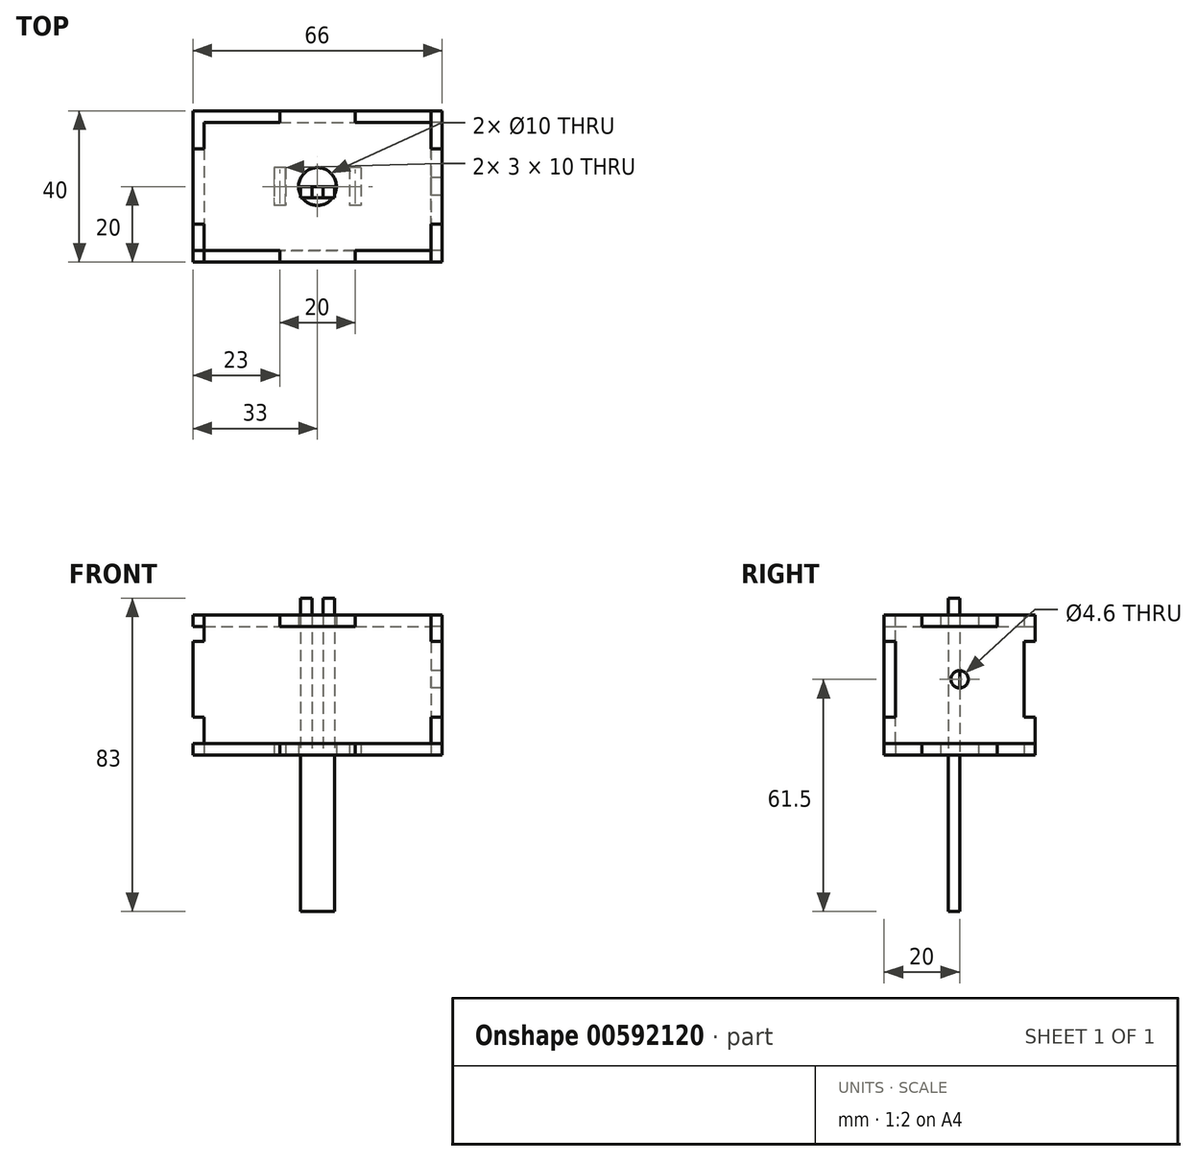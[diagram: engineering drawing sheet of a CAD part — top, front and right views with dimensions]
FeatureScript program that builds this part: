
annotation { "Feature Type Name" : "Feature", "Feature Type Description" : "" }
export const myFeature = defineFeature(function(context is Context, id is Id, definition is map)
    precondition{}
    {
        {
            var Q0;
            Q0=qCreatedBy(makeId("Top.planeOp"),FACE);
            var sketch = newSketch(context, id + "F0", { "sketchPlane" : qUnion([Q0])});
            skLineSegment(sketch, "E0.bottom", {"start": v(33, 20) * mm, "end": v(-33, 20) * mm});
            skLineSegment(sketch, "E0.top", {"start": v(33, -20) * mm, "end": v(-33, -20) * mm});
            skLineSegment(sketch, "E0.left", {"start": v(33, 20) * mm, "end": v(33, -20) * mm});
            skLineSegment(sketch, "E0.right", {"start": v(-33, 20) * mm, "end": v(-33, -20) * mm});
            skLineSegment(sketch, "E1.bottom", {"start": v(-10, 20) * mm, "end": v(10, 20) * mm});
            skLineSegment(sketch, "E1.top", {"start": v(-10, 17) * mm, "end": v(10, 17) * mm});
            skLineSegment(sketch, "E1.left", {"start": v(-10, 20) * mm, "end": v(-10, 17) * mm});
            skLineSegment(sketch, "E1.right", {"start": v(10, 20) * mm, "end": v(10, 17) * mm});
            skLineSegment(sketch, "E2.bottom", {"start": v(33, 10) * mm, "end": v(30, 10) * mm});
            skLineSegment(sketch, "E2.top", {"start": v(33, -10) * mm, "end": v(30, -10) * mm});
            skLineSegment(sketch, "E2.left", {"start": v(33, 10) * mm, "end": v(33, -10) * mm});
            skLineSegment(sketch, "E2.right", {"start": v(30, 10) * mm, "end": v(30, -10) * mm});
            skLineSegment(sketch, "E3.bottom", {"start": v(10, -20) * mm, "end": v(-10, -20) * mm});
            skLineSegment(sketch, "E3.top", {"start": v(10, -17) * mm, "end": v(-10, -17) * mm});
            skLineSegment(sketch, "E3.left", {"start": v(10, -20) * mm, "end": v(10, -17) * mm});
            skLineSegment(sketch, "E3.right", {"start": v(-10, -20) * mm, "end": v(-10, -17) * mm});
            skLineSegment(sketch, "E4.bottom", {"start": v(-33, 10) * mm, "end": v(-30, 10) * mm});
            skLineSegment(sketch, "E4.top", {"start": v(-33, -10) * mm, "end": v(-30, -10) * mm});
            skLineSegment(sketch, "E4.left", {"start": v(-33, 10) * mm, "end": v(-33, -10) * mm});
            skLineSegment(sketch, "E4.right", {"start": v(-30, 10) * mm, "end": v(-30, -10) * mm});
            skPoint(sketch, "E5", {"position": v(-30, 0) * mm});
            skPoint(sketch, "E6", {"position": v(0, 17) * mm});
            skPoint(sketch, "E7", {"position": v(0, -17) * mm});
            skPoint(sketch, "E8", {"position": v(30, 0) * mm});
            skCircle(sketch, "E9", {"center": v(0, 0) * mm, "radius": 5 * mm});
            skLineSegment(sketch, "E10.bottom", {"start": v(-8.5, 5) * mm, "end": v(-11.5, 5) * mm});
            skLineSegment(sketch, "E10.top", {"start": v(-8.5, -5) * mm, "end": v(-11.5, -5) * mm});
            skLineSegment(sketch, "E10.left", {"start": v(-8.5, 5) * mm, "end": v(-8.5, -5) * mm});
            skLineSegment(sketch, "E10.right", {"start": v(-11.5, 5) * mm, "end": v(-11.5, -5) * mm});
            skPoint(sketch, "E10.middle", {"position": v(-10, 0) * mm});
            skLineSegment(sketch, "E11.bottom", {"start": v(11.5, 5) * mm, "end": v(8.5, 5) * mm});
            skLineSegment(sketch, "E11.top", {"start": v(11.5, -5) * mm, "end": v(8.5, -5) * mm});
            skLineSegment(sketch, "E11.left", {"start": v(11.5, 5) * mm, "end": v(11.5, -5) * mm});
            skLineSegment(sketch, "E11.right", {"start": v(8.5, 5) * mm, "end": v(8.5, -5) * mm});
            skPoint(sketch, "E11.middle", {"position": v(10, 0) * mm});
            skSolve(sketch);
        }
        {
            var Q0;
            Q0=makeQuery(id+"F0.imprint","IMPRINT",FACE,{"disambiguationData":[TD([[makeQuery(id+"F0.imprint","IMPRINT",EDGE,{"derivedFrom":sQuery(id+"F0.wireOp",EDGE,"E0.bottom")}),1.0]])]});
            extrude(context, id + "F1", {"entities" : qUnion([Q0]), "depth" : 3 * mm, "offsetDistance" : 25 * mm});
        }
        {
            var Q0;
            Q0=makeQuery(id+"F1.opExtrude","SWEPT_FACE",FACE,{"disambiguationData":[OSD([sQuery(id+"F0.wireOp",EDGE,"E2.right")])]});
            var sketch = newSketch(context, id + "F2", { "sketchPlane" : qUnion([Q0])});
            skLineSegment(sketch, "E12.bottom", {"start": v(-20, 3) * mm, "end": v(20, 3) * mm});
            skLineSegment(sketch, "E12.top", {"start": v(-20, 37) * mm, "end": v(20, 37) * mm});
            skLineSegment(sketch, "E12.left", {"start": v(-20, 3) * mm, "end": v(-20, 37) * mm});
            skLineSegment(sketch, "E12.right", {"start": v(20, 3) * mm, "end": v(20, 37) * mm});
            skLineSegment(sketch, "E13.bottom", {"start": v(-10, 3) * mm, "end": v(10, 3) * mm});
            skLineSegment(sketch, "E13.top", {"start": v(-10, 0) * mm, "end": v(10, 0) * mm});
            skLineSegment(sketch, "E13.left", {"start": v(-10, 3) * mm, "end": v(-10, 0) * mm});
            skLineSegment(sketch, "E13.right", {"start": v(10, 3) * mm, "end": v(10, 0) * mm});
            skCircle(sketch, "E14", {"center": v(0, 20) * mm, "radius": 2.3 * mm});
            skLineSegment(sketch, "E15.bottom", {"start": v(20, 30) * mm, "end": v(17, 30) * mm});
            skLineSegment(sketch, "E15.top", {"start": v(20, 10) * mm, "end": v(17, 10) * mm});
            skLineSegment(sketch, "E15.left", {"start": v(20, 30) * mm, "end": v(20, 10) * mm});
            skLineSegment(sketch, "E15.right", {"start": v(17, 30) * mm, "end": v(17, 10) * mm});
            skLineSegment(sketch, "E16.bottom", {"start": v(-20, 30) * mm, "end": v(-17, 30) * mm});
            skLineSegment(sketch, "E16.top", {"start": v(-20, 10) * mm, "end": v(-17, 10) * mm});
            skLineSegment(sketch, "E16.left", {"start": v(-20, 30) * mm, "end": v(-20, 10) * mm});
            skLineSegment(sketch, "E16.right", {"start": v(-17, 30) * mm, "end": v(-17, 10) * mm});
            skLineSegment(sketch, "E17.bottom", {"start": v(10, 37) * mm, "end": v(-10, 37) * mm});
            skLineSegment(sketch, "E17.top", {"start": v(10, 34) * mm, "end": v(-10, 34) * mm});
            skLineSegment(sketch, "E17.left", {"start": v(10, 37) * mm, "end": v(10, 34) * mm});
            skLineSegment(sketch, "E17.right", {"start": v(-10, 37) * mm, "end": v(-10, 34) * mm});
            skPoint(sketch, "E18", {"position": v(0, 34) * mm});
            skPoint(sketch, "E19", {"position": v(17, 20) * mm});
            skPoint(sketch, "E20", {"position": v(-17, 20) * mm});
            skSolve(sketch);
        }
        {
            var Q0;
            Q0=makeQuery(id+"F2.imprint","IMPRINT",FACE,{"disambiguationData":[TD([[makeQuery(id+"F2.imprint","IMPRINT",EDGE,{"derivedFrom":sQuery(id+"F2.wireOp",EDGE,"E12.top")}),-1.0]])]});
            var Q1;
            Q1=makeQuery(id+"F2.imprint","IMPRINT",FACE,{"disambiguationData":[TD([[makeQuery(id+"F2.imprint","IMPRINT",EDGE,{"derivedFrom":sQuery(id+"F2.wireOp",EDGE,"E13.bottom")}),1.0]])]});
            extrude(context, id + "F3", {"entities" : qUnion([Q0, Q1]), "depth" : 3 * mm, "offsetDistance" : 25 * mm});
        }
        {
            var Q0;
            Q0=qCreatedBy(makeId("Front.planeOp"),FACE);
            var sketch = newSketch(context, id + "F4", { "sketchPlane" : qUnion([Q0])});
            skLineSegment(sketch, "E21.bottom", {"start": v(4.5, 41.5) * mm, "end": v(-4.5, 41.5) * mm});
            skLineSegment(sketch, "E21.top", {"start": v(4.5, -41.5) * mm, "end": v(-4.5, -41.5) * mm});
            skLineSegment(sketch, "E21.left", {"start": v(4.5, 41.5) * mm, "end": v(4.5, -41.5) * mm});
            skLineSegment(sketch, "E21.right", {"start": v(-4.5, 41.5) * mm, "end": v(-4.5, -41.5) * mm});
            skPoint(sketch, "E21.middle", {"position": v(0, 0) * mm});
            skLineSegment(sketch, "E22.bottom", {"start": v(-1.5, 41.5) * mm, "end": v(1.5, 41.5) * mm});
            skLineSegment(sketch, "E22.top", {"start": v(-1.5, 0) * mm, "end": v(1.5, 0) * mm});
            skLineSegment(sketch, "E22.left", {"start": v(-1.5, 41.5) * mm, "end": v(-1.5, 0) * mm});
            skLineSegment(sketch, "E22.right", {"start": v(1.5, 41.5) * mm, "end": v(1.5, 0) * mm});
            skSolve(sketch);
        }
        {
            var Q0;
            Q0=makeQuery(id+"F4.imprint","IMPRINT",FACE,{"disambiguationData":[TD([[makeQuery(id+"F4.imprint","IMPRINT",EDGE,{"derivedFrom":sQuery(id+"F4.wireOp",EDGE,"E21.top")}),-1.0]])]});
            extrude(context, id + "F5", {"entities" : qUnion([Q0]), "depth" : 3 * mm, "offsetDistance" : 25 * mm});
        }
        {
            var Q0;
            Q0=makeQuery(id+"F3.opExtrude","SWEPT_FACE",FACE,{"disambiguationData":[OSD([sQuery(id+"F2.wireOp",EDGE,"E17.top")])]});
            var sketch = newSketch(context, id + "F6", { "sketchPlane" : qUnion([Q0])});
            skLineSegment(sketch, "E23.bottom", {"start": v(-30, -17) * mm, "end": v(30, -17) * mm});
            skLineSegment(sketch, "E23.top", {"start": v(-30, 17) * mm, "end": v(30, 17) * mm});
            skLineSegment(sketch, "E23.left", {"start": v(-30, -17) * mm, "end": v(-30, 17) * mm});
            skLineSegment(sketch, "E23.right", {"start": v(30, -17) * mm, "end": v(30, 17) * mm});
            skLineSegment(sketch, "E24.bottom", {"start": v(10, 17) * mm, "end": v(-10, 17) * mm});
            skLineSegment(sketch, "E24.top", {"start": v(10, 20) * mm, "end": v(-10, 20) * mm});
            skLineSegment(sketch, "E24.left", {"start": v(10, 17) * mm, "end": v(10, 20) * mm});
            skLineSegment(sketch, "E24.right", {"start": v(-10, 17) * mm, "end": v(-10, 20) * mm});
            skLineSegment(sketch, "E25.bottom", {"start": v(10, -17) * mm, "end": v(-10, -17) * mm});
            skLineSegment(sketch, "E25.top", {"start": v(10, -20) * mm, "end": v(-10, -20) * mm});
            skLineSegment(sketch, "E25.left", {"start": v(10, -17) * mm, "end": v(10, -20) * mm});
            skLineSegment(sketch, "E25.right", {"start": v(-10, -17) * mm, "end": v(-10, -20) * mm});
            skLineSegment(sketch, "E26.bottom", {"start": v(30, -10) * mm, "end": v(33, -10) * mm});
            skLineSegment(sketch, "E26.top", {"start": v(30, 10) * mm, "end": v(33, 10) * mm});
            skLineSegment(sketch, "E26.left", {"start": v(30, -10) * mm, "end": v(30, 10) * mm});
            skLineSegment(sketch, "E26.right", {"start": v(33, -10) * mm, "end": v(33, 10) * mm});
            skLineSegment(sketch, "E27.bottom", {"start": v(-30, 10) * mm, "end": v(-33, 10) * mm});
            skLineSegment(sketch, "E27.top", {"start": v(-30, -10) * mm, "end": v(-33, -10) * mm});
            skLineSegment(sketch, "E27.left", {"start": v(-30, 10) * mm, "end": v(-30, -10) * mm});
            skLineSegment(sketch, "E27.right", {"start": v(-33, 10) * mm, "end": v(-33, -10) * mm});
            skCircle(sketch, "E28", {"center": v(0, 0) * mm, "radius": 5 * mm});
            skSolve(sketch);
        }
        {
            var Q0;
            Q0=qSketchRegion(id+"F6",true);
            extrude(context, id + "F7", {"entities" : qUnion([Q0]), "depth" : 3 * mm, "offsetDistance" : 25 * mm});
        }
        {
            var Q0;
            Q0=makeQuery(id+"F3.opExtrude","SWEPT_FACE",FACE,{"disambiguationData":[OSD([sQuery(id+"F2.wireOp",EDGE,"E16.right")])]});
            var sketch = newSketch(context, id + "F8", { "sketchPlane" : qUnion([Q0])});
            skLineSegment(sketch, "E29.bottom", {"start": v(-30, 3) * mm, "end": v(30, 3) * mm});
            skLineSegment(sketch, "E29.top", {"start": v(-30, 37) * mm, "end": v(30, 37) * mm});
            skLineSegment(sketch, "E29.left", {"start": v(-30, 3) * mm, "end": v(-30, 37) * mm});
            skLineSegment(sketch, "E29.right", {"start": v(30, 3) * mm, "end": v(30, 37) * mm});
            skLineSegment(sketch, "E30.bottom", {"start": v(10, 37) * mm, "end": v(-10, 37) * mm});
            skLineSegment(sketch, "E30.top", {"start": v(10, 34) * mm, "end": v(-10, 34) * mm});
            skLineSegment(sketch, "E30.left", {"start": v(10, 34) * mm, "end": v(10, 37) * mm});
            skLineSegment(sketch, "E30.right", {"start": v(-10, 34) * mm, "end": v(-10, 37) * mm});
            skLineSegment(sketch, "E31.bottom", {"start": v(-30, 30) * mm, "end": v(-33, 30) * mm});
            skLineSegment(sketch, "E31.top", {"start": v(-30, 10) * mm, "end": v(-33, 10) * mm});
            skLineSegment(sketch, "E31.left", {"start": v(-30, 30) * mm, "end": v(-30, 10) * mm});
            skLineSegment(sketch, "E31.right", {"start": v(-33, 30) * mm, "end": v(-33, 10) * mm});
            skLineSegment(sketch, "E32.bottom", {"start": v(-10, 3) * mm, "end": v(10, 3) * mm});
            skLineSegment(sketch, "E32.top", {"start": v(-10, 0) * mm, "end": v(10, 0) * mm});
            skLineSegment(sketch, "E32.left", {"start": v(-10, 3) * mm, "end": v(-10, 0) * mm});
            skLineSegment(sketch, "E32.right", {"start": v(10, 3) * mm, "end": v(10, 0) * mm});
            skLineSegment(sketch, "E33.bottom", {"start": v(30, 10) * mm, "end": v(33, 10) * mm});
            skLineSegment(sketch, "E33.top", {"start": v(30, 30) * mm, "end": v(33, 30) * mm});
            skLineSegment(sketch, "E33.left", {"start": v(30, 10) * mm, "end": v(30, 30) * mm});
            skLineSegment(sketch, "E33.right", {"start": v(33, 10) * mm, "end": v(33, 30) * mm});
            skSolve(sketch);
        }
        {
            var Q0;
            Q0=makeQuery(id+"F8.imprint","IMPRINT",FACE,{"disambiguationData":[TD([[makeQuery(id+"F8.imprint","IMPRINT",EDGE,{"derivedFrom":sQuery(id+"F8.wireOp",EDGE,"E30.top")}),1.0]])]});
            var Q1;
            Q1=makeQuery(id+"F8.imprint","IMPRINT",FACE,{"disambiguationData":[TD([[makeQuery(id+"F8.imprint","IMPRINT",EDGE,{"derivedFrom":sQuery(id+"F8.wireOp",EDGE,"E31.bottom")}),1.0]])]});
            var Q2;
            Q2=makeQuery(id+"F8.imprint","IMPRINT",FACE,{"disambiguationData":[TD([[makeQuery(id+"F8.imprint","IMPRINT",EDGE,{"derivedFrom":sQuery(id+"F8.wireOp",EDGE,"E32.bottom")}),-1.0]])]});
            var Q3;
            Q3=makeQuery(id+"F8.imprint","IMPRINT",FACE,{"disambiguationData":[TD([[makeQuery(id+"F8.imprint","IMPRINT",EDGE,{"derivedFrom":sQuery(id+"F8.wireOp",EDGE,"E33.bottom")}),-1.0]])]});
            extrude(context, id + "F9", {"entities" : qUnion([Q0, Q1, Q2, Q3]), "depth" : 3 * mm, "offsetDistance" : 25 * mm});
        }
    });
